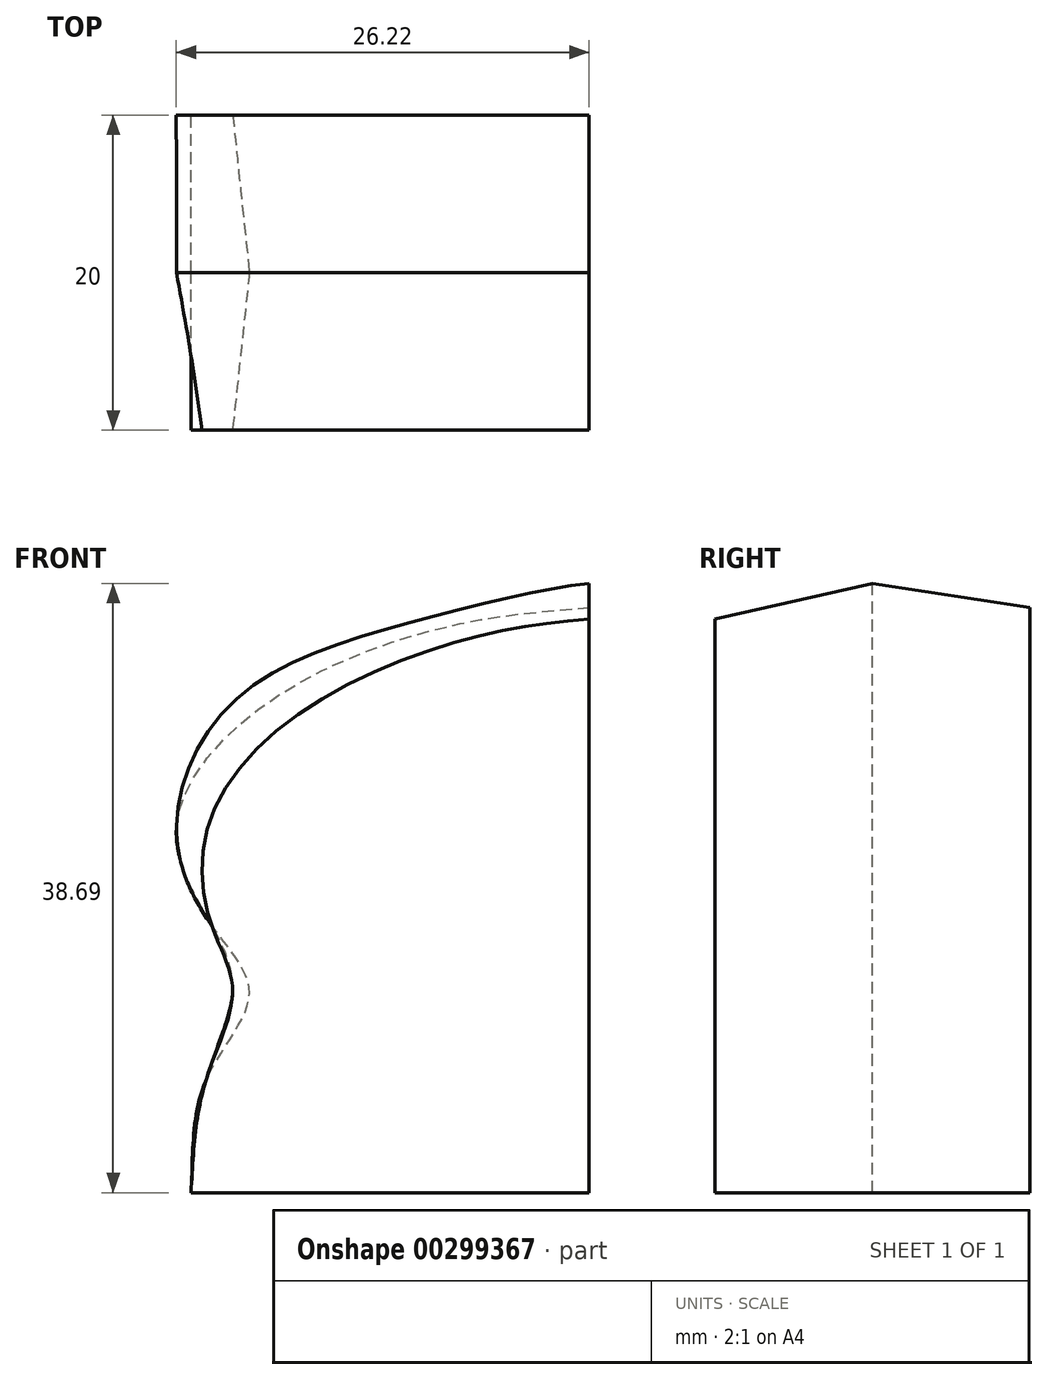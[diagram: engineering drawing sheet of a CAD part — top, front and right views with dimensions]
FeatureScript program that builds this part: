
annotation { "Feature Type Name" : "Feature", "Feature Type Description" : "" }
export const myFeature = defineFeature(function(context is Context, id is Id, definition is map)
    precondition{}
    {
        {
            var Q0;
            Q0=qCreatedBy(makeId("Front.planeOp"),FACE);
            cPlane(context, id + "F0", {"entities" : qUnion([Q0]), "cplaneType" : CPlaneType.OFFSET, "offset" : 10 * mm, "width" : 150 * mm, "height" : 150 * mm});
        }
        {
            var Q0;
            Q0=qCreatedBy(id+"F0.planeOp",FACE);
            cPlane(context, id + "F1", {"entities" : qUnion([Q0]), "cplaneType" : CPlaneType.OFFSET, "offset" : 10 * mm, "width" : 150 * mm, "height" : 150 * mm});
        }
        {
            var Q0;
            Q0=qCreatedBy(id+"F1.planeOp",FACE);
            var sketch = newSketch(context, id + "F2", { "sketchPlane" : qUnion([Q0])});
            skFitSpline(sketch, "E0", {"points": [v(-25.28, 0) * mm, v(-24.36, 7.06) * mm, v(-22.64, 12.74) * mm, v(-23.96, 16.96) * mm, v(-24.22, 23.2) * mm, v(-18.57, 30.32) * mm, v(-7.53, 35.24) * mm, v(0, 36.45) * mm], "startDerivative": vector(3, 52.43) * mm, "endDerivative": vector(49.65, 4.76) * mm});
            skLineSegment(sketch, "E1", {"start": v(-25.28, 0) * mm, "end": v(0, 0) * mm});
            skLineSegment(sketch, "E2", {"start": v(0, 36.45) * mm, "end": v(0, 0) * mm});
            skFitSpline(sketch, "E3.MirrorCS", {"points": [v(25.28, 0) * mm, v(24.36, 7.06) * mm, v(22.64, 12.74) * mm, v(23.96, 16.96) * mm, v(24.22, 23.2) * mm, v(18.57, 30.32) * mm, v(7.53, 35.24) * mm, v(0, 36.45) * mm], "startDerivative": vector(-3, 52.43) * mm, "endDerivative": vector(-49.65, 4.76) * mm});
            skLineSegment(sketch, "E4.MirrorCS", {"start": v(25.28, 0) * mm, "end": v(0, 0) * mm});
            skSolve(sketch);
        }
        {
            var Q0;
            Q0=qCreatedBy(id+"F0.planeOp",FACE);
            var sketch = newSketch(context, id + "F3", { "sketchPlane" : qUnion([Q0])});
            skFitSpline(sketch, "E5", {"points": [v(-25.28, 0) * mm, v(-24.36, 7.06) * mm, v(-21.58, 12.58) * mm, v(-23.96, 16.96) * mm, v(-26.2, 23.2) * mm, v(-22.54, 31.24) * mm, v(-11.3, 36.24) * mm, v(0, 38.69) * mm], "startDerivative": vector(3, 52.43) * mm, "endDerivative": vector(49.65, 4.76) * mm});
            skLineSegment(sketch, "E6", {"start": v(-25.28, 0) * mm, "end": v(0, 0) * mm});
            skLineSegment(sketch, "E7", {"start": v(0, 38.69) * mm, "end": v(0, 0) * mm});
            skFitSpline(sketch, "E8.MirrorCS", {"points": [v(25.28, 0) * mm, v(24.36, 7.06) * mm, v(21.58, 12.58) * mm, v(23.96, 16.96) * mm, v(26.2, 23.2) * mm, v(22.54, 31.24) * mm, v(11.3, 36.24) * mm, v(0, 38.69) * mm], "startDerivative": vector(-3, 52.43) * mm, "endDerivative": vector(-49.65, 4.76) * mm});
            skLineSegment(sketch, "E9.MirrorCS", {"start": v(25.28, 0) * mm, "end": v(0, 0) * mm});
            skSolve(sketch);
        }
        {
            var Q0;
            Q0=qCreatedBy(makeId("Front.planeOp"),FACE);
            var sketch = newSketch(context, id + "F4", { "sketchPlane" : qUnion([Q0])});
            skFitSpline(sketch, "E10", {"points": [v(-25.28, 0) * mm, v(-24.36, 7.06) * mm, v(-22.64, 12.74) * mm, v(-23.96, 16.96) * mm, v(-26.2, 23.2) * mm, v(-20.27, 31.24) * mm, v(-7.72, 36.24) * mm, v(0, 37.16) * mm], "startDerivative": vector(3, 52.43) * mm, "endDerivative": vector(49.65, 4.76) * mm});
            skLineSegment(sketch, "E11", {"start": v(-25.28, 0) * mm, "end": v(0, 0) * mm});
            skLineSegment(sketch, "E12", {"start": v(0, 37.16) * mm, "end": v(0, 0) * mm});
            skFitSpline(sketch, "E13.MirrorCS", {"points": [v(25.28, 0) * mm, v(24.36, 7.06) * mm, v(22.64, 12.74) * mm, v(23.96, 16.96) * mm, v(26.2, 23.2) * mm, v(20.27, 31.24) * mm, v(7.72, 36.24) * mm, v(0, 37.16) * mm], "startDerivative": vector(-3, 52.43) * mm, "endDerivative": vector(-49.65, 4.76) * mm});
            skLineSegment(sketch, "E14.MirrorCS", {"start": v(25.28, 0) * mm, "end": v(0, 0) * mm});
            skSolve(sketch);
        }
        {
            var Q0;
            Q0=makeQuery(id+"F2.imprint","IMPRINT",FACE,{"disambiguationData":[TD([[makeQuery(id+"F2.imprint","IMPRINT",EDGE,{"derivedFrom":sQuery(id+"F2.wireOp",EDGE,"E0")}),-1.0]])]});
            var Q1;
            Q1=makeQuery(id+"F3.imprint","IMPRINT",FACE,{"disambiguationData":[TD([[makeQuery(id+"F3.imprint","IMPRINT",EDGE,{"derivedFrom":sQuery(id+"F3.wireOp",EDGE,"E5")}),-1.0]])]});
            loft(context, id + "F5", {"sheetProfilesArray" : [{ "sheetProfileEntities" : qUnion([Q0]) }, { "sheetProfileEntities" : qUnion([Q1]) }]});
        }
        {
            var Q1;
            Q1=makeQuery(id+"F3.imprint","IMPRINT",FACE,{"disambiguationData":[TD([[makeQuery(id+"F3.imprint","IMPRINT",EDGE,{"derivedFrom":sQuery(id+"F3.wireOp",EDGE,"E5")}),-1.0]])]});
            var Q2;
            Q2=makeQuery(id+"F4.imprint","IMPRINT",FACE,{"disambiguationData":[TD([[makeQuery(id+"F4.imprint","IMPRINT",EDGE,{"derivedFrom":sQuery(id+"F4.wireOp",EDGE,"E10")}),-1.0]])]});
            loft(context, id + "F6", {"operationType" : NewBodyOperationType.ADD, "sheetProfilesArray" : [{ "sheetProfileEntities" : qUnion([Q1]) }, { "sheetProfileEntities" : qUnion([Q2]) }]});
        }
    });
